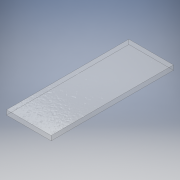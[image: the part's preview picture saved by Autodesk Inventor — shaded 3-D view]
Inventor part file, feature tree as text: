
AUTODESK INVENTOR PART (.ipt)
format: ipt  version: 2019 (Build 230136000, 136)  size: 109,056 bytes
history: native  units: mm
features: extrude x1, sketch x1
ambient origin geometry x8: Origin, YZ Plane, XZ Plane, XY Plane, X Axis, Y Axis, Z Axis, Center Point
bodies: Solid1 (feature_tree)
feature tree (2):
  extrude  "Extrusion1"  Depth=58.0mm
  sketch  "Sketch1"  dims[d0=159.0mm d1=58.0mm d2=6.0mm d3=0.0mm]
